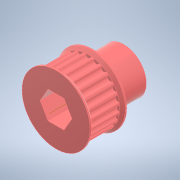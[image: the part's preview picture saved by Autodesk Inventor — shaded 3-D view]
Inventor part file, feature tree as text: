
AUTODESK INVENTOR PART (.ipt)
format: ipt  version: 2022.3 (Build 263350000, 350)  size: 322,048 bytes
history: native  units: in
note: dims shown in document units (in); Inventor stores cm internally (conversion verified against a paired STEP export)
features: extrude x7, sketch x7, mirror x2, chamfer x2, other x1, fillet x1, pattern_circular x1, projected_geometry x1
ambient origin geometry x8: Origin, YZ Plane, XZ Plane, XY Plane, X Axis, Y Axis, Z Axis, Center Point
bodies: Solid1 (feature_tree)
feature tree (22):
  other  "Hex Bore"
  extrude  "HTD Base"  Depth=0.3937in TaperAngle=0.0deg
  extrude  "HTD Flange"  Depth=0.0591in
  mirror  "HTD Flanges"
  chamfer  "HTD Flange Chamfer"  Distance=0.0787in Angle=45.0deg
  extrude  "GT2 Base"  TaperAngle=0.0deg  [1 undecoded]
  extrude  "GT2 Base Tooth"  TaperAngle=0.0deg  [1 undecoded]
  fillet  "GT2 Base Tooth pt. 2"  Radius=0.8723in
  pattern_circular  "GT2 Teeth"  [2 undecoded]
  extrude  "GT2 Flange"  Depth=0.4375in
  mirror  "GT2 Flanges"
  chamfer  "GT2 Flange Chamfer"  Distance=0.0075in
  extrude  "Circle Bore"  TaperAngle=0.0deg  [1 undecoded]
  extrude  "Extrusion9"  Depth=0.0118in
  sketch  "Sketch1"  dims[d0=1.4588in d1=0.3937in d2=0.0in]
  sketch  "Sketch4"  dims[d12=0.0394in d13=0.0591in]
  sketch  "Sketch5"  dims[d14=0.0in]
  sketch  "Sketch6"  dims[d15=0.0394in d16=0.0787in d17=45.0deg]
  sketch  "Sketch7"  dims[d18=0.385in d19=0.0in d20=0.0in]
  sketch  "Sketch8"  dims[d21=0.385in d22=0.0in d23=0.0in d24=0.8723in]
  sketch  "Sketch9"  dims[d25=0.3937in d26=0.0in d27=0.0727in d28=0.0075in d29=0.0in d30=0.0in d31=0.0118in d32=9.4488in d33=360.0deg d35=0.0394in d36=0.0591in d37=0.0in d38=0.0394in d39=0.0787in d40=45.0deg d41=0.625in d42=0.4375in d43=0.0in]
  projected_geometry  "Projected Loop1"
note: 5 required parameter values undecoded (feature->parameter linkage not recoverable at this tier; creation-order binding heuristic only, values carry confidence <= 0.55)
